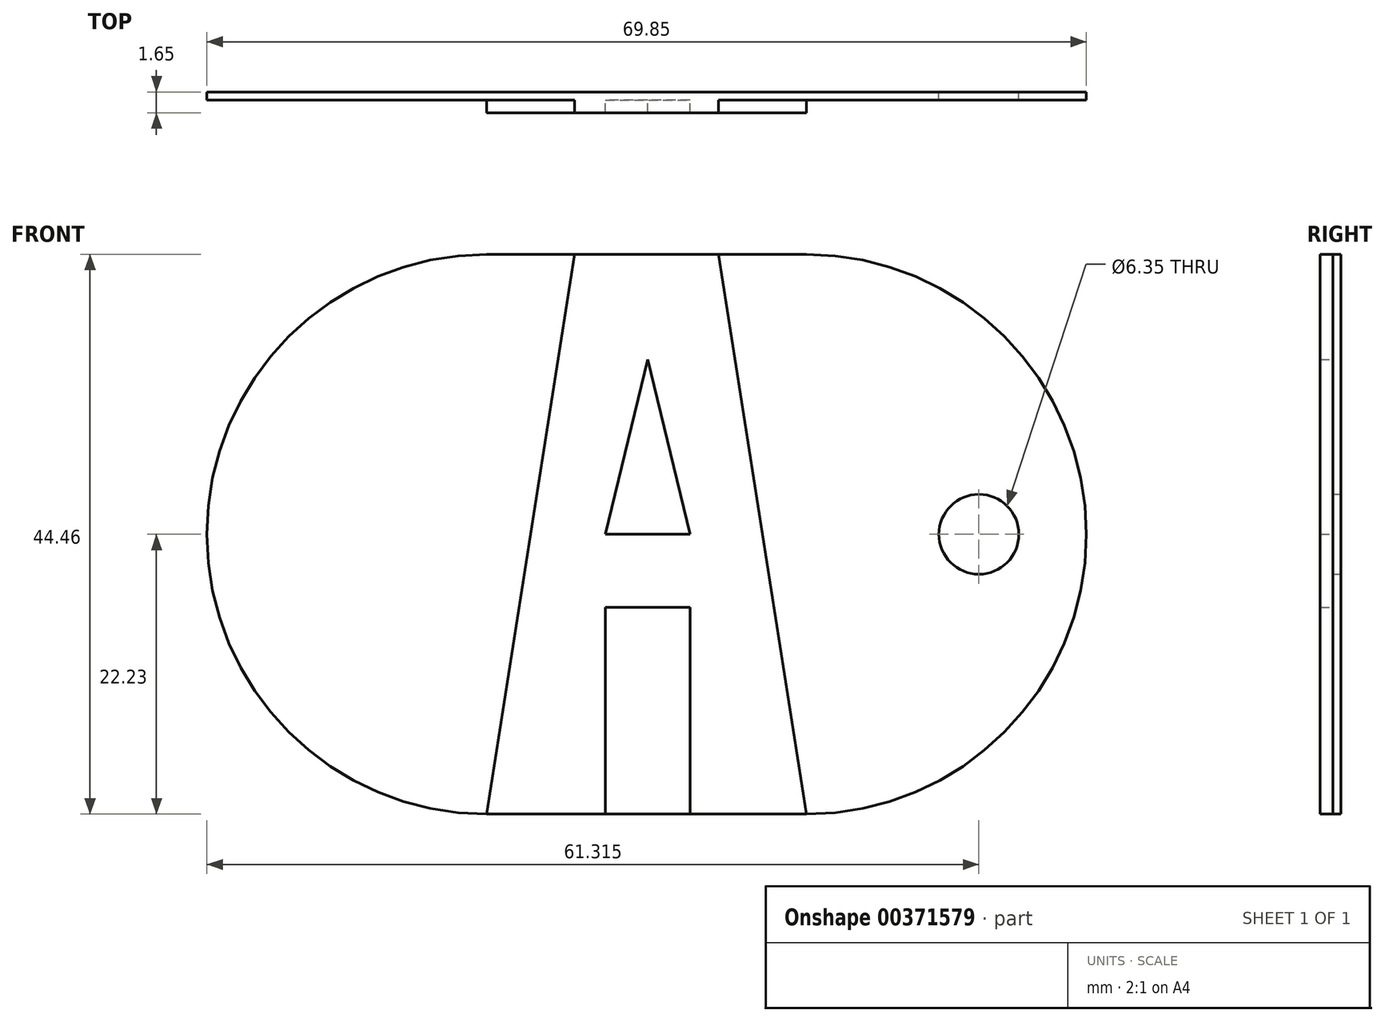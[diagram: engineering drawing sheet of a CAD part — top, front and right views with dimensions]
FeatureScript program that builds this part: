
annotation { "Feature Type Name" : "Feature", "Feature Type Description" : "" }
export const myFeature = defineFeature(function(context is Context, id is Id, definition is map)
    precondition{}
    {
        {
            var Q0;
            Q0=qCreatedBy(makeId("Front.planeOp"),FACE);
            var sketch = newSketch(context, id + "F0", { "sketchPlane" : qUnion([Q0])});
            skArc(sketch, "E0", {"start": v(3, 22.23) * mm, "mid": v(-19.22, 0) * mm, "end": v(3, -22.23) * mm});
            skArc(sketch, "E1", {"start": v(28.4, -22.23) * mm, "mid": v(50.63, 0) * mm, "end": v(28.4, 22.23) * mm});
            skLineSegment(sketch, "E2", {"start": v(3, 22.23) * mm, "end": v(28.4, 22.23) * mm});
            skLineSegment(sketch, "E3", {"start": v(3, -22.23) * mm, "end": v(28.4, -22.23) * mm});
            skCircle(sketch, "E4", {"center": v(42.1, 0) * mm, "radius": 3.18 * mm});
            skSolve(sketch);
        }
        {
            var Q0;
            Q0 = qSketchRegion(id + "F0", true);
            extrude(context, id + "F1", {"entities" : qUnion([Q0]), "depth" : 0.64 * mm});
        }
        {
            var Q0;
            Q0=makeQuery(id+"F1.opExtrude","CAP_FACE",FACE,{"disambiguationData":[OSD([sQuery(id+"F0.wireOp",EDGE,"E0"),sQuery(id+"F0.wireOp",EDGE,"E1"),sQuery(id+"F0.wireOp",EDGE,"E2"),sQuery(id+"F0.wireOp",EDGE,"E3"),sQuery(id+"F0.wireOp",EDGE,"E4")])],"isStart":false});
            var sketch = newSketch(context, id + "F2", { "sketchPlane" : qUnion([Q0])});
            skLineSegment(sketch, "E5", {"start": v(3, -22.23) * mm, "end": v(9.98, 22.23) * mm});
            skLineSegment(sketch, "E6", {"start": v(9.98, 22.23) * mm, "end": v(21.42, 22.23) * mm});
            skLineSegment(sketch, "E7", {"start": v(21.42, 22.23) * mm, "end": v(28.4, -22.23) * mm});
            skLineSegment(sketch, "E8", {"start": v(12.41, -22.23) * mm, "end": v(12.41, -5.8) * mm});
            skLineSegment(sketch, "E9", {"start": v(12.41, -5.8) * mm, "end": v(19.16, -5.8) * mm});
            skLineSegment(sketch, "E10", {"start": v(19.16, -5.8) * mm, "end": v(19.16, -22.23) * mm});
            skLineSegment(sketch, "E11", {"start": v(12.41, 0) * mm, "end": v(19.16, 0) * mm});
            skLineSegment(sketch, "E12", {"start": v(19.16, 0) * mm, "end": v(15.79, 13.9) * mm});
            skPoint(sketch, "E12.endSnap0", {"position": v(15.79, 0) * mm});
            skLineSegment(sketch, "E13", {"start": v(15.79, 13.9) * mm, "end": v(12.41, 0) * mm});
            skSolve(sketch);
        }
        {
            var Q0;
            {var subQ1=sQuery(id+"F2.wireOp",EDGE,"E5");Q0=makeQuery(id+"F2.imprint","IMPRINT",FACE,{"disambiguationData":[TD([[makeQuery(id+"F2.imprint","IMPRINT",EDGE,{"derivedFrom":subQ1}),-1.0]])]});}
            extrude(context, id + "F3", {"entities" : qUnion([Q0]), "operationType" : NewBodyOperationType.ADD, "depth" : 1.02 * mm});
        }
    });
